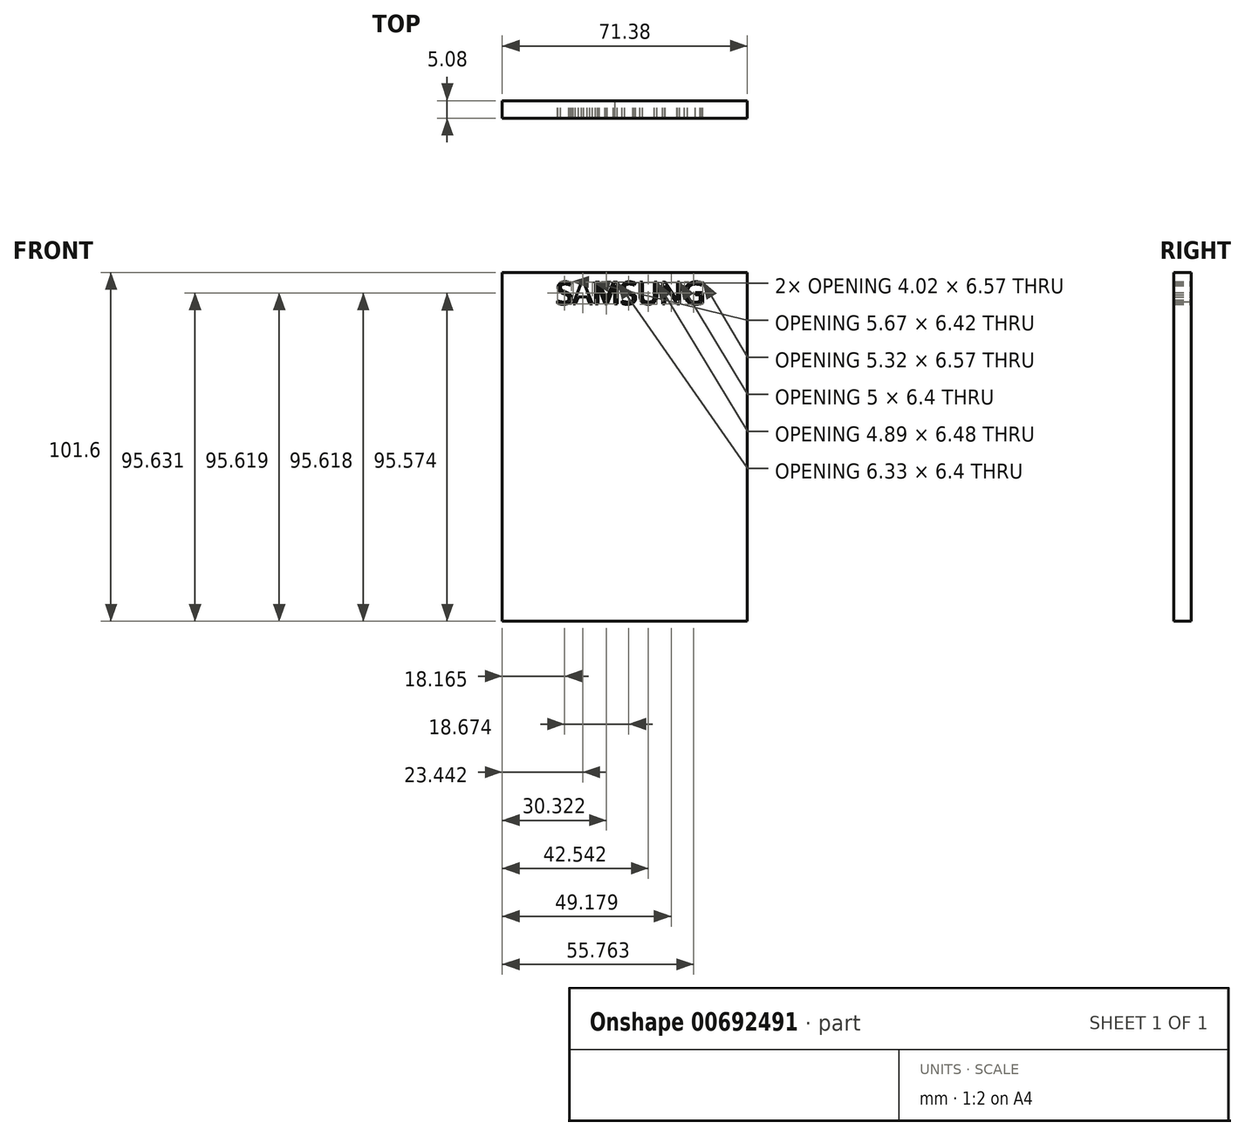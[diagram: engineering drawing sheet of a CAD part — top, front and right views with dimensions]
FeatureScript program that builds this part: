
annotation { "Feature Type Name" : "Feature", "Feature Type Description" : "" }
export const myFeature = defineFeature(function(context is Context, id is Id, definition is map)
    precondition{}
    {
        {
            var Q0;
            Q0=qCreatedBy(makeId("Front.planeOp"),FACE);
            var sketch = newSketch(context, id + "F0", { "sketchPlane" : qUnion([Q0])});
            skLineSegment(sketch, "E0.bottom", {"start": v(-35.5, 50.8) * mm, "end": v(35.88, 50.8) * mm});
            skLineSegment(sketch, "E0.top", {"start": v(-35.5, -50.8) * mm, "end": v(35.88, -50.8) * mm});
            skLineSegment(sketch, "E0.left", {"start": v(-35.5, 50.8) * mm, "end": v(-35.5, -50.8) * mm});
            skLineSegment(sketch, "E0.right", {"start": v(35.88, 50.8) * mm, "end": v(35.88, -50.8) * mm});
            skLineSegment(sketch, "E1.left", {"start": v(-128.26, 63.04) * mm, "end": v(-128.26, 62.66) * mm});
            skLineSegment(sketch, "E1.right", {"start": v(-122.57, 63.04) * mm, "end": v(-122.57, 62.66) * mm});
            skText(sketch, "E2", { "text": "SAMSUNG\n", "fontName": "OpenSans-Regular.ttf"});
            skPoint(sketch, "E3", {"position": v(0, 50.8) * mm});
            const initialGuessF0  = {"E2": [-0.01981, 0.04162, 1, 0, 0.00645]};
            skSetInitialGuess(sketch, initialGuessF0);
            skSolve(sketch);
        }
        {
            var Q0;
            Q0 = qSketchRegion(id + "F0", true);
            extrude(context, id + "F1", {"entities" : qUnion([Q0]), "depth" : 5.08 * mm, "offsetDistance" : 25.4 * mm});
        }
    });
